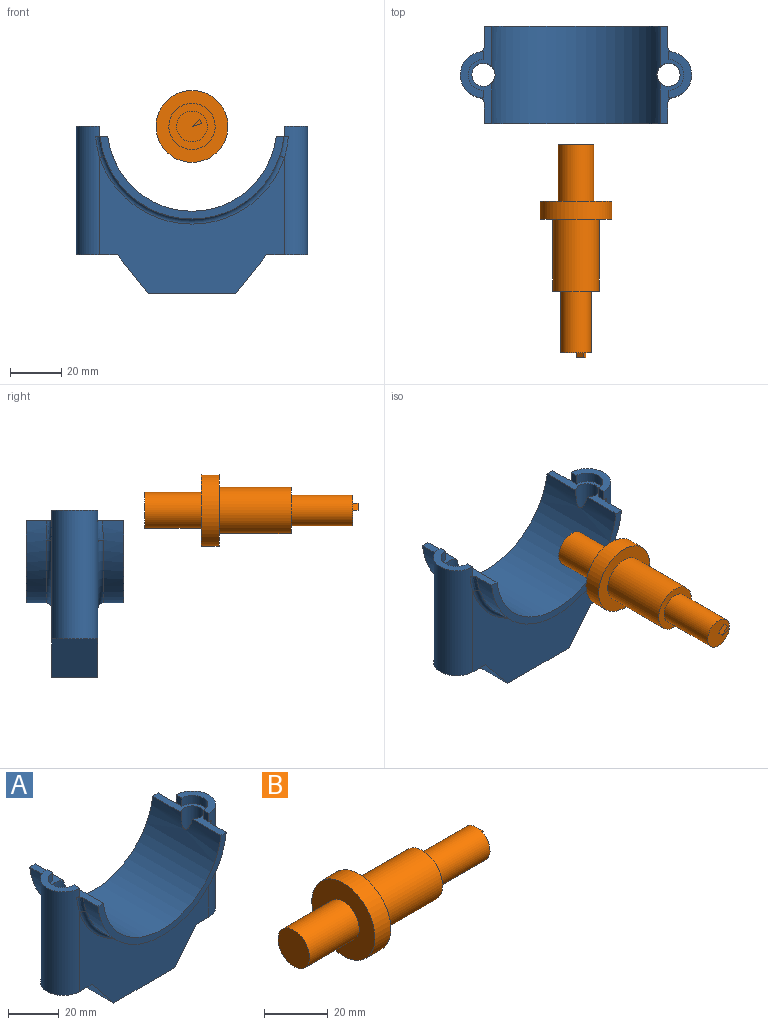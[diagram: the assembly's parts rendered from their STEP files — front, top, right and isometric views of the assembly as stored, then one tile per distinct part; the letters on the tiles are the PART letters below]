
ASSEMBLY  parts=2 mates=1
PART A: 32 faces, bbox 90.1x38.1x65.1 mm
  f0: plane 18x9mm, normal (0,0,1), area 70.7mm2, adj f4,f5,f24,f28
  f1: plane 18x9mm, normal (0,0,1), area 70.7mm2, adj f2,f3,f25,f27
  f2: plane 4x3mm, normal (-1,0,0), area 12mm2, adj f1,f25,f26,f27
  f3: plane 4x3mm, normal (-1,0,0), area 12mm2, adj f1,f25,f26,f27
  f4: plane 4x3mm, normal (1,0,0), area 12mm2, adj f0,f24,f28,f29
  f5: plane 4x3mm, normal (1,0,0), area 12mm2, adj f0,f24,f28,f29
  f6: bspline ~13.94x4.21mm, area 23.5mm2, adj f15,f24,f29,f30
  f7: bspline ~13.94x4.21mm, area 23.5mm2, adj f15,f25,f26,f30
  f8: bspline ~13.94x4.21mm, area 23.5mm2, adj f14,f24,f29,f31
  f9: bspline ~13.94x4.21mm, area 23.5mm2, adj f14,f25,f26,f31
  f10: cylinder r=33mm len=65.51mm, axis (0,-1,0), area 3588.6mm2, adj f13,f16,f17,f18,f26,f29
  f11: plane 72x52.83mm, normal (0,1,0), area 2054.4mm2, adj f19,f20,f21,f22,f23,f24,f25,f30
  f12: plane 72x52.83mm, normal (0,-1,0), area 2054.4mm2, adj f19,f20,f21,f22,f23,f24,f25,f31
  f13: plane 71.55x32mm, normal (0,-1,0), area 301.1mm2, adj f10,f14,f26,f29
  f14: cylinder r=36mm len=71.55mm, axis (0,1,0), area 841.7mm2, adj f8,f9,f13,f26,f29,f31
  f15: cylinder r=36mm len=71.55mm, axis (0,1,0), area 841.7mm2, adj f6,f7,f16,f26,f29,f30
  f16: plane 71.55x32mm, normal (0,1,0), area 301.1mm2, adj f10,f15,f26,f29
  f17: cylinder r=4.5mm len=46mm, axis (0,0,1), area 1271.8mm2, adj f10,f20,f26
  f18: cylinder r=4.5mm len=46mm, axis (0,0,1), area 1280.5mm2, adj f10,f19,f29
  f19: plane 18x16mm, normal (0,0,-1), area 189.6mm2, adj f11,f12,f18,f23,f24
  f20: plane 18x16mm, normal (0,0,-1), area 189.6mm2, adj f11,f12,f17,f22,f25
  f21: plane 34x18mm, normal (0,0,-1), area 612mm2, adj f11,f12,f22,f23
  f22: plane 18x15mm, normal (0.78,0,-0.62), area 345.8mm2, adj f11,f12,f20,f21
  f23: plane 18x15mm, normal (-0.78,0,-0.62), area 345.8mm2, adj f11,f12,f19,f21
  f24: cylinder r=9mm len=50mm, axis (0,0,1), area 1401.7mm2, adj f0,f4,f5,f6,f8,f11,f12,f19
  f25: cylinder r=9mm len=50mm, axis (0,0,1), area 1401.7mm2, adj f1,f2,f3,f7,f9,f11,f12,f20
  f26: plane 38.07x9.32mm, normal (0,0,1), area 118.5mm2, adj f2,f3,f7,f9,f10,f13,f14,f15
  f27: cylinder r=6mm len=12mm, axis (0,0,1), area 75.4mm2, adj f1,f2,f3,f26
  f28: cylinder r=6mm len=12mm, axis (0,0,1), area 75.4mm2, adj f0,f4,f5,f29
  f29: plane 38.07x9.32mm, normal (0,0,1), area 118.5mm2, adj f4,f5,f6,f8,f10,f13,f14,f15
  f30: torus R=38mm, axis (0,-1,0), area 287.3mm2, adj f6,f7,f11,f15
  f31: torus R=38mm, axis (0,-1,0), area 287.3mm2, adj f8,f9,f12,f14
PART B: 13 faces, bbox 83x28x28 mm
  f0: plane 12x12mm, normal (1,0,0), area 109.4mm2, adj f1,f9,f10,f11
  f1: cylinder r=6mm len=24mm, axis (-1,0,0), area 904.8mm2, adj f0,f2
  f2: plane 18x18mm, normal (1,0,0), area 141.4mm2, adj f1,f3
  f3: cylinder r=9mm len=28mm, axis (-1,0,0), area 1583.4mm2, adj f2,f4
  f4: plane 28x28mm, normal (1,0,0), area 361.3mm2, adj f3,f5
  f5: cylinder r=14mm len=28mm, axis (-1,0,0), area 615.8mm2, adj f4,f6
  f6: plane 28x28mm, normal (-1,0,0), area 461.8mm2, adj f5,f7
  f7: cylinder r=7mm len=22mm, axis (-1,0,0), area 967.6mm2, adj f6,f8
  f8: plane 14x14mm, normal (-1,0,0), area 153.9mm2, adj f7
  f9: plane 2x1.87mm, normal (0,0,1), area 3.7mm2, adj f0,f10,f11,f12
  f10: plane 3.95x2mm, normal (0,-0.97,-0.23), area 8.1mm2, adj f0,f9,f11,f12
  f11: plane 3.95x2mm, normal (0,0.97,-0.23), area 8.1mm2, adj f0,f9,f10,f12
  f12: plane 3.95x1.87mm, normal (1,0,0), area 3.7mm2, adj f9,f10,f11
PLACE A at identity fixed
PLACE B rot(axis=(-0.45,0.45,-0.77),104.5deg) t=(0,-99.17,65)mm
MATE cylindrical B.f1 <-> A.f10  axis (0,-1,0) through (0,-47.17,65)mm
